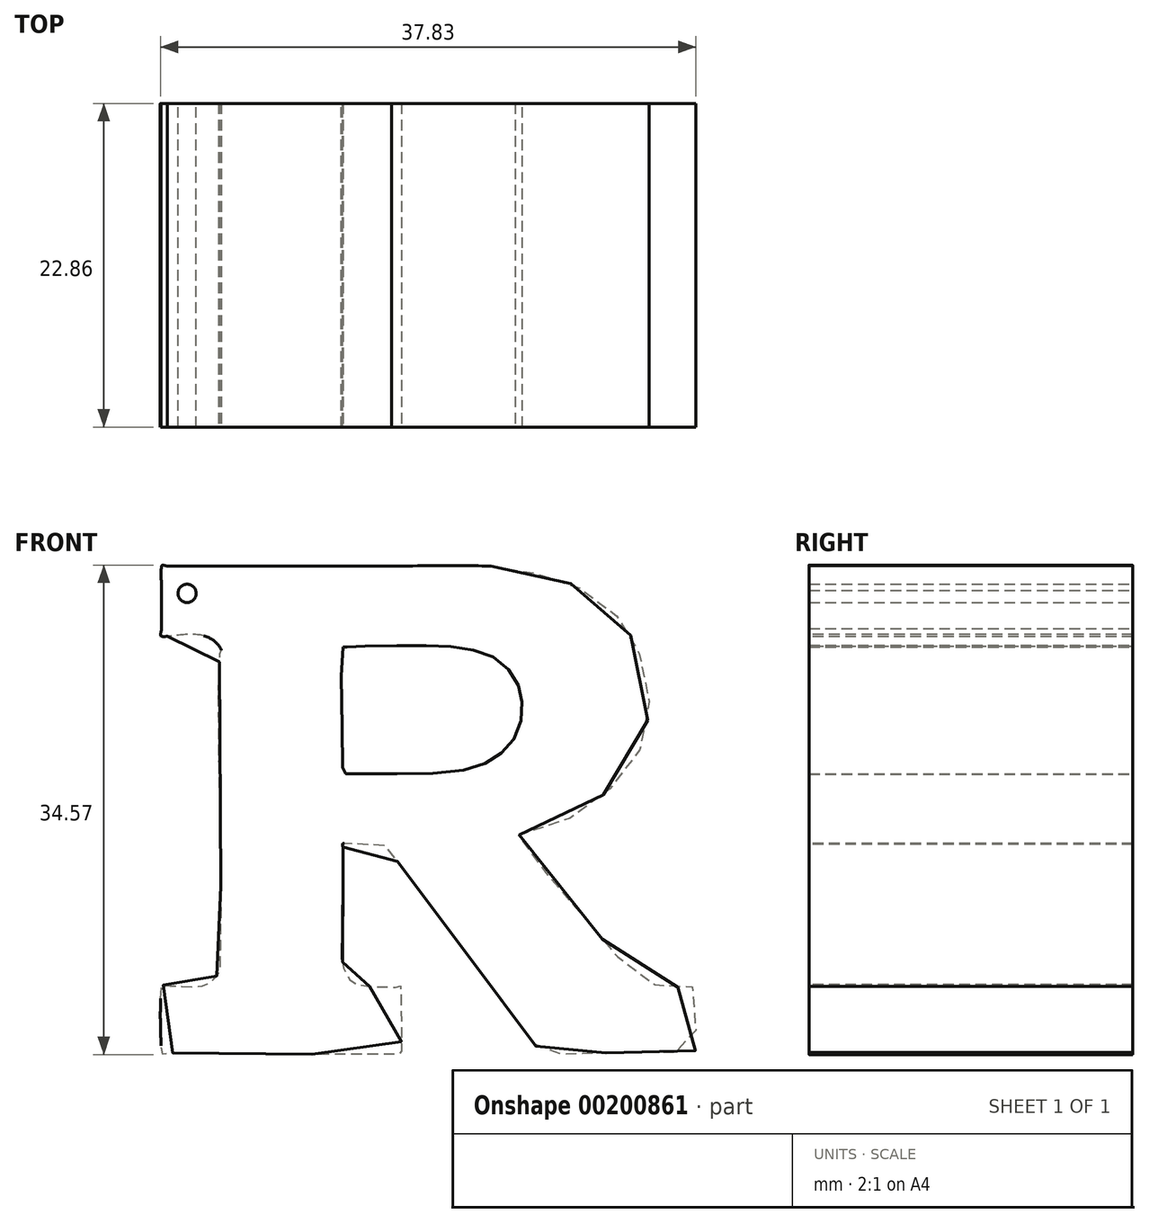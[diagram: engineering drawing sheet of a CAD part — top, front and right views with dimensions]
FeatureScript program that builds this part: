
annotation { "Feature Type Name" : "Feature", "Feature Type Description" : "" }
export const myFeature = defineFeature(function(context is Context, id is Id, definition is map)
    precondition{}
    {
        {
            var Q0;
            Q0=qCreatedBy(makeId("Front.planeOp"),FACE);
            var sketch = newSketch(context, id + "F0", { "sketchPlane" : qUnion([Q0])});
            skLineSegment(sketch, "E0", {"start": v(-81.1, 22.81) * mm, "end": v(-81.1, 17.86) * mm});
            skLineSegment(sketch, "E1", {"start": v(-81.1, 17.86) * mm, "end": v(-78.51, 17.86) * mm});
            skLineSegment(sketch, "E2", {"start": v(-81.1, 22.81) * mm, "end": v(-80.7, 22.81) * mm});
            skPoint(sketch, "E3.54.internal.snap0", {"position": v(-79.8, 17.86) * mm});
            skFitSpline(sketch, "E3", {"points": [v(-57.83, 22.81) * mm, v(-54.9, 22.37) * mm, v(-52.34, 21.63) * mm, v(-49.56, 19.9) * mm, v(-48.18, 18.27) * mm, v(-46.87, 15.22) * mm, v(-46.75, 12.1) * mm, v(-47.79, 8.92) * mm, v(-50.1, 6.5) * mm, v(-53.07, 4.64) * mm, v(-56.1, 3.73) * mm, v(-56.03, 3.6) * mm, v(-48.26, -5.46) * mm, v(-46.37, -6.73) * mm, v(-44.18, -6.92) * mm, v(-43.43, -6.89) * mm, v(-43.39, -6.94) * mm, v(-43.4, -11.54) * mm, v(-43.45, -11.56) * mm, v(-48.42, -11.54) * mm, v(-50.74, -11.59) * mm, v(-54.36, -11.64) * mm, v(-54.41, -11.54) * mm, v(-56.62, -8.5) * mm, v(-59.58, -4.5) * mm, v(-63.43, 0.65) * mm, v(-65.37, 3.15) * mm, v(-65.39, 3.15) * mm, v(-68.3, 3.23) * mm, v(-68.32, 3.17) * mm, v(-68.32, -2.87) * mm, v(-68.28, -5.48) * mm, v(-68.2, -5.64) * mm, v(-68.03, -6.09) * mm, v(-67.4, -6.7) * mm, v(-66.2, -6.86) * mm, v(-64.26, -6.86) * mm, v(-64.22, -6.82) * mm, v(-64.16, -11.62) * mm, v(-64.18, -11.66) * mm, v(-68.36, -11.66) * mm, v(-78.52, -11.6) * mm, v(-80.98, -11.65) * mm, v(-81.06, -11.65) * mm, v(-81.06, -6.76) * mm, v(-80.98, -6.76) * mm, v(-80.92, -6.78) * mm, v(-78.98, -6.9) * mm, v(-77.77, -6.65) * mm, v(-77.01, -5.86) * mm, v(-76.96, -5.43) * mm, v(-76.9, -0.93) * mm, v(-76.94, 16.77) * mm, v(-76.89, 16.87) * mm, v(-77.97, 17.86) * mm, v(-81.1, 17.86) * mm, v(-81.1, 18.4) * mm, v(-81.1, 22.81) * mm, v(-80.7, 22.81) * mm, v(-57.83, 22.81) * mm]});
            skLineSegment(sketch, "E4.trimOffspring", {"start": v(-64.84, 22.81) * mm, "end": v(-57.83, 22.81) * mm});
            skLineSegment(sketch, "E5", {"start": v(-80.7, 22.81) * mm, "end": v(-64.84, 22.81) * mm});
            skFitSpline(sketch, "E6", {"points": [v(-68.28, 17.11) * mm, v(-68.3, 8.3) * mm, v(-68.28, 8.16) * mm, v(-66.76, 8.16) * mm, v(-60.22, 8.32) * mm, v(-57.55, 9.3) * mm, v(-56.08, 10.8) * mm, v(-55.62, 12.97) * mm, v(-56.03, 14.66) * mm, v(-57.47, 16.3) * mm, v(-60.09, 17.06) * mm, v(-64, 17.22) * mm, v(-67.98, 17.11) * mm, v(-68.07, 17.1) * mm, v(-68.19, 17.13) * mm, v(-68.28, 17.11) * mm]});
            skCircle(sketch, "E7", {"center": v(-79.3, 20.9) * mm, "radius": 0.65 * mm});
            skLineSegment(sketch, "E8", {"start": v(-81.1, -13.77) * mm, "end": v(-43.72, -13.77) * mm});
            skLineSegment(sketch, "E9", {"start": v(-83.86, 22.81) * mm, "end": v(-83.86, -13.77) * mm});
            skSolve(sketch);
        }
        {
            var Q0;
            Q0 = qSketchRegion(id + "F0", true);
            extrude(context, id + "F1", {"entities" : qUnion([Q0]), "depth" : 22.86 * mm});
        }
    });
